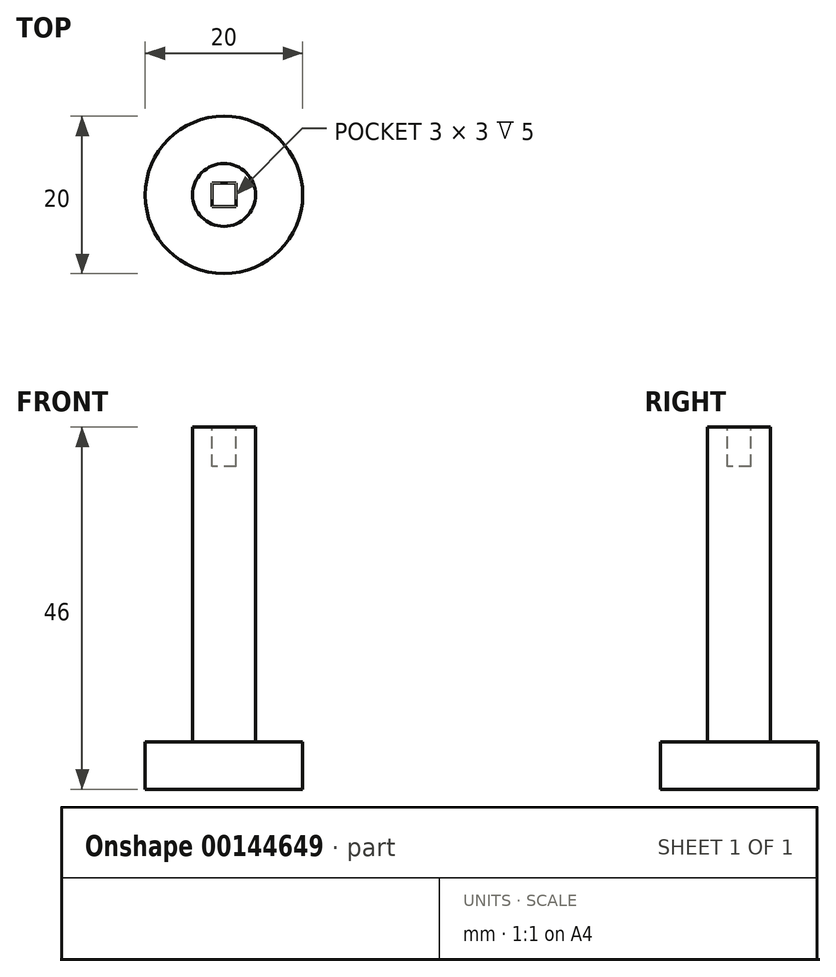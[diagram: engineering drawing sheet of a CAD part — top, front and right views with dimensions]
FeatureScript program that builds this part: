
annotation { "Feature Type Name" : "Feature", "Feature Type Description" : "" }
export const myFeature = defineFeature(function(context is Context, id is Id, definition is map)
    precondition{}
    {
        {
            var Q0;
            Q0=qCreatedBy(makeId("Top.planeOp"),FACE);
            var sketch = newSketch(context, id + "F0", { "sketchPlane" : qUnion([Q0])});
            skCircle(sketch, "E0", {"center": v(0, 0) * mm, "radius": 10 * mm});
            skSolve(sketch);
        }
        {
            var Q0;
            Q0=makeQuery(id+"F0.imprint","IMPRINT",FACE,{"disambiguationData":[TD([[makeQuery(id+"F0.imprint","IMPRINT",EDGE,{"derivedFrom":sQuery(id+"F0.wireOp",EDGE,"E0")}),1.0]])]});
            extrude(context, id + "F1", {"entities" : qUnion([Q0]), "depth" : 6 * mm});
        }
        {
            var Q0;
            Q0=makeQuery(id+"F1.opExtrude","CAP_FACE",FACE,{"disambiguationData":[OSD([sQuery(id+"F0.wireOp",EDGE,"E0")])],"isStart":false});
            var sketch = newSketch(context, id + "F2", { "sketchPlane" : qUnion([Q0])});
            skCircle(sketch, "E1", {"center": v(0, 0) * mm, "radius": 4 * mm});
            skSolve(sketch);
        }
        {
            var Q0;
            Q0=makeQuery(id+"F2.imprint","IMPRINT",FACE,{"disambiguationData":[TD([[makeQuery(id+"F2.imprint","IMPRINT",EDGE,{"derivedFrom":sQuery(id+"F2.wireOp",EDGE,"E1")}),1.0]])]});
            extrude(context, id + "F3", {"entities" : qUnion([Q0]), "operationType" : NewBodyOperationType.ADD, "depth" : 40 * mm});
        }
        {
            var Q0;
            Q0=makeQuery(id+"F3.opExtrude","CAP_FACE",FACE,{"disambiguationData":[OSD([sQuery(id+"F2.wireOp",EDGE,"E1")])],"isStart":false});
            var sketch = newSketch(context, id + "F4", { "sketchPlane" : qUnion([Q0])});
            skLineSegment(sketch, "E2.bottom", {"start": v(1.5, 1.5) * mm, "end": v(-1.5, 1.5) * mm});
            skLineSegment(sketch, "E2.top", {"start": v(1.5, -1.5) * mm, "end": v(-1.5, -1.5) * mm});
            skLineSegment(sketch, "E2.left", {"start": v(1.5, 1.5) * mm, "end": v(1.5, -1.5) * mm});
            skLineSegment(sketch, "E2.right", {"start": v(-1.5, 1.5) * mm, "end": v(-1.5, -1.5) * mm});
            skPoint(sketch, "E2.middle", {"position": v(0, 0) * mm});
            skSolve(sketch);
        }
        {
            var Q0;
            Q0=makeQuery(id+"F4.imprint","IMPRINT",FACE,{"disambiguationData":[TD([[makeQuery(id+"F4.imprint","IMPRINT",EDGE,{"derivedFrom":sQuery(id+"F4.wireOp",EDGE,"E2.bottom")}),1.0]])]});
            extrude(context, id + "F5", {"entities" : qUnion([Q0]), "operationType" : NewBodyOperationType.REMOVE, "oppositeDirection" : true, "depth" : 5 * mm});
        }
    });
